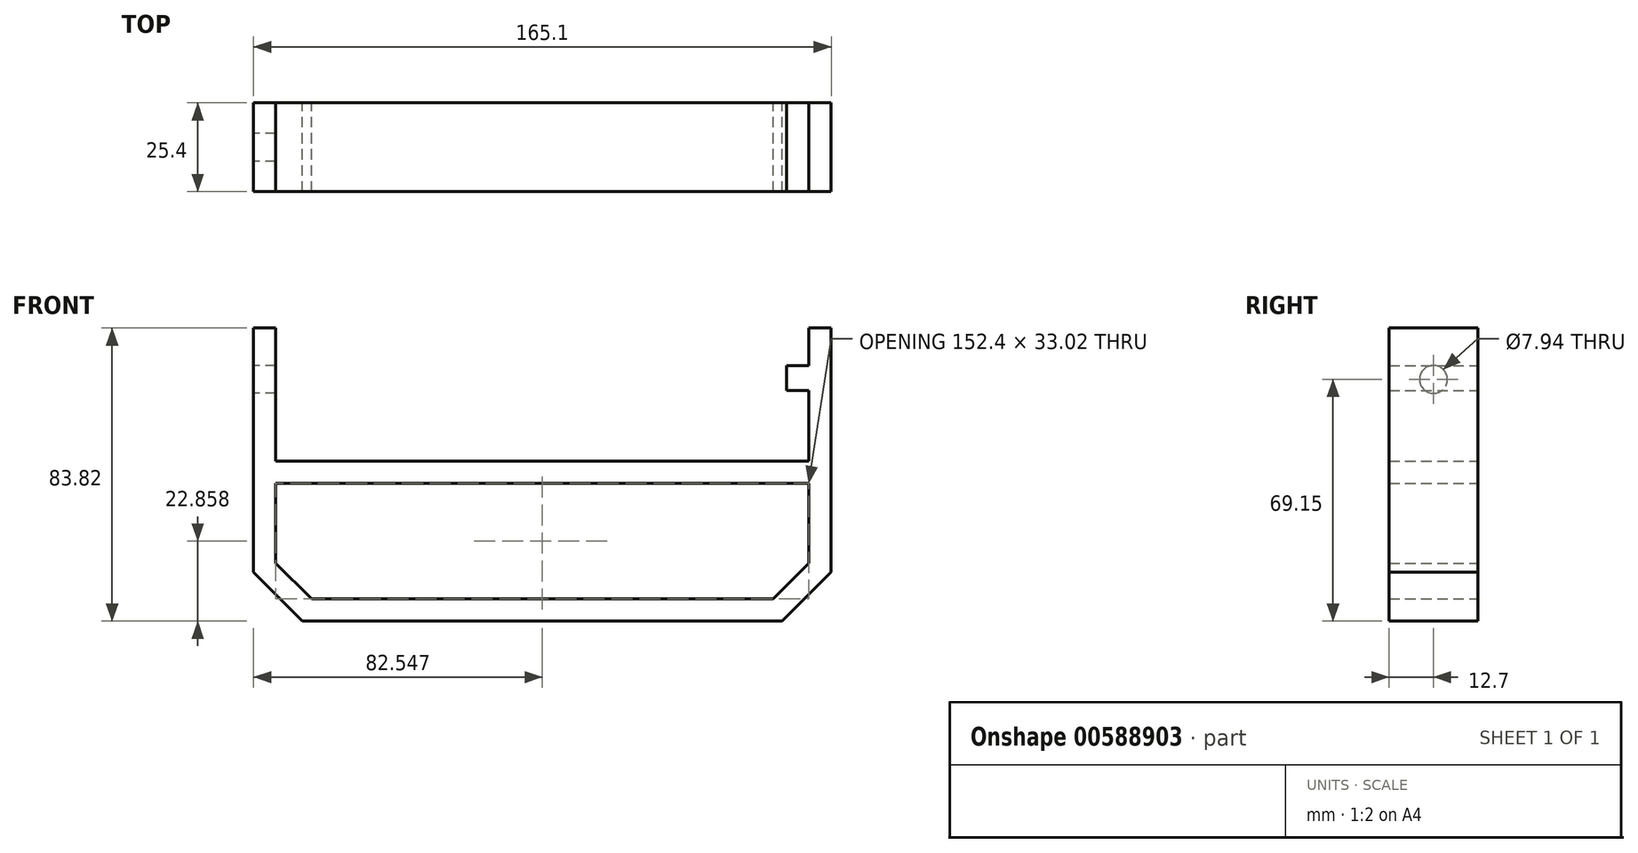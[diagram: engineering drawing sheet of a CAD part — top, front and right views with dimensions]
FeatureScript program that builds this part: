
annotation { "Feature Type Name" : "Feature", "Feature Type Description" : "" }
export const myFeature = defineFeature(function(context is Context, id is Id, definition is map)
    precondition{}
    {
        {
            var Q0;
            Q0=qCreatedBy(makeId("Front.planeOp"),FACE);
            var sketch = newSketch(context, id + "F0", { "sketchPlane" : qUnion([Q0])});
            skLineSegment(sketch, "E0.top", {"start": v(-69.02, -38.86) * mm, "end": v(68.14, -38.86) * mm});
            skLineSegment(sketch, "E0.left", {"start": v(-76.64, 44.96) * mm, "end": v(-76.64, 34.26) * mm});
            skLineSegment(sketch, "E0.right", {"start": v(75.76, 44.96) * mm, "end": v(75.76, 34.21) * mm});
            skLineSegment(sketch, "E1", {"start": v(-76.64, 34.26) * mm, "end": v(-83, 34.26) * mm});
            skLineSegment(sketch, "E2", {"start": v(-76.64, 26.31) * mm, "end": v(-83, 26.31) * mm});
            skLineSegment(sketch, "E3.trimOffspring", {"start": v(-76.64, 26.31) * mm, "end": v(-76.64, 6.86) * mm});
            skLineSegment(sketch, "E4.trimOffspring", {"start": v(75.76, 27.1) * mm, "end": v(75.76, 6.86) * mm});
            skLineSegment(sketch, "E5", {"start": v(-83, -24.9) * mm, "end": v(-69.02, -38.86) * mm});
            skLineSegment(sketch, "E6", {"start": v(68.14, -38.86) * mm, "end": v(82.1, -24.9) * mm});
            skLineSegment(sketch, "E7", {"start": v(-76.64, 6.86) * mm, "end": v(75.76, 6.86) * mm});
            skLineSegment(sketch, "E8", {"start": v(75.76, 44.96) * mm, "end": v(82.1, 44.96) * mm});
            skLineSegment(sketch, "E9", {"start": v(82.1, 44.96) * mm, "end": v(82.1, -24.9) * mm});
            skLineSegment(sketch, "E10", {"start": v(-76.64, 44.96) * mm, "end": v(-83, 44.96) * mm});
            skLineSegment(sketch, "E11", {"start": v(-83, 44.96) * mm, "end": v(-83, -24.9) * mm});
            skLineSegment(sketch, "E12.bottom", {"start": v(75.76, 34.21) * mm, "end": v(69.36, 34.21) * mm});
            skLineSegment(sketch, "E12.top", {"start": v(75.76, 27.1) * mm, "end": v(69.36, 27.1) * mm});
            skLineSegment(sketch, "E12.right", {"start": v(69.36, 34.21) * mm, "end": v(69.36, 27.1) * mm});
            skLineSegment(sketch, "E13.0", {"start": v(-76.64, -22.26) * mm, "end": v(-66.4, -32.51) * mm});
            skLineSegment(sketch, "E14.0", {"start": v(65.5, -32.51) * mm, "end": v(75.76, -22.26) * mm});
            skLineSegment(sketch, "E15.0", {"start": v(-66.4, -32.51) * mm, "end": v(65.5, -32.51) * mm});
            skLineSegment(sketch, "E16.0", {"start": v(-76.64, 0.5) * mm, "end": v(75.76, 0.5) * mm});
            skLineSegment(sketch, "E17.trimOffspring", {"start": v(-76.64, 0.5) * mm, "end": v(-76.64, -22.26) * mm});
            skLineSegment(sketch, "E18.trimOffspring", {"start": v(75.76, 0.5) * mm, "end": v(75.76, -22.26) * mm});
            skLineSegment(sketch, "E19", {"start": v(-76.64, 34.26) * mm, "end": v(-76.64, 26.31) * mm});
            skLineSegment(sketch, "E20", {"start": v(-76.64, 30.29) * mm, "end": v(-83, 30.29) * mm});
            skSolve(sketch);
        }
        {
            var Q0;
            Q0=makeQuery(id+"F0.imprint","IMPRINT",FACE,{"disambiguationData":[TD([[makeQuery(id+"F0.imprint","IMPRINT",EDGE,{"derivedFrom":sQuery(id+"F0.wireOp",EDGE,"E0.top")}),1.0]])]});
            var Q1;
            Q1=makeQuery(id+"F0.imprint","IMPRINT",FACE,{"disambiguationData":[TD([[makeQuery(id+"F0.imprint","IMPRINT",EDGE,{"derivedFrom":sQuery(id+"F0.wireOp",EDGE,"E0.left")}),-1.0]])]});
            var Q2;
            {var subQ0=sQuery(id+"F0.wireOp",EDGE,"E1");Q2=makeQuery(id+"F0.imprint","IMPRINT",FACE,{"disambiguationData":[TD([[makeQuery(id+"F0.imprint","IMPRINT",EDGE,{"derivedFrom":subQ0}),1.0]])]});}
            var Q3;
            {var subQ0=sQuery(id+"F0.wireOp",EDGE,"E2");Q3=makeQuery(id+"F0.imprint","IMPRINT",FACE,{"disambiguationData":[TD([[makeQuery(id+"F0.imprint","IMPRINT",EDGE,{"derivedFrom":subQ0}),-1.0]])]});}
            extrude(context, id + "F1", {"entities" : qUnion([Q0, Q1, Q2, Q3]), "depth" : 25.4 * mm, "offsetDistance" : 25.4 * mm});
        }
        {
            var Q0;
            Q0=makeQuery(id+"F1.opExtrude","SWEPT_FACE",FACE,{"disambiguationData":[OSD([sQuery(id+"F0.wireOp",EDGE,"E11")])]});
            var sketch = newSketch(context, id + "F2", { "sketchPlane" : qUnion([Q0])});
            skLineSegment(sketch, "E21", {"start": v(12.7, 44.96) * mm, "end": v(12.7, 15.62) * mm});
            skCircle(sketch, "E22", {"center": v(12.7, 30.29) * mm, "radius": 3.97 * mm});
            skSolve(sketch);
        }
        {
            var Q0;
            {var subQ0=sQuery(id+"F2.wireOp",EDGE,"E22");var subQ1=sQuery(id+"F2.wireOp",EDGE,"E21");var subQ2=makeQuery(id+"F2.imprint","INTERSECT",VERTEX,{"disambiguationData":[OD(0.0)],"derivedFrom":[subQ1,subQ0]});Q0=makeQuery(id+"F2.imprint","IMPRINT",FACE,{"disambiguationData":[TD([[makeQuery(id+"F2.imprint","IMPRINT",EDGE,{"disambiguationData":[TD([[subQ2,1.0]])],"derivedFrom":subQ1}),-1.0]])]});}
            var Q1;
            {var subQ0=sQuery(id+"F2.wireOp",EDGE,"E22");var subQ1=sQuery(id+"F2.wireOp",EDGE,"E21");var subQ2=makeQuery(id+"F2.imprint","INTERSECT",VERTEX,{"disambiguationData":[OD(0.0)],"derivedFrom":[subQ1,subQ0]});Q1=makeQuery(id+"F2.imprint","IMPRINT",FACE,{"disambiguationData":[TD([[makeQuery(id+"F2.imprint","IMPRINT",EDGE,{"disambiguationData":[TD([[subQ2,1.0]])],"derivedFrom":subQ1}),1.0]])]});}
            extrude(context, id + "F3", {"entities" : qUnion([Q0, Q1]), "operationType" : NewBodyOperationType.REMOVE, "oppositeDirection" : true, "depth" : 25.4 * mm, "offsetDistance" : 25.4 * mm});
        }
    });
